# Revit family: Shower-Bath-American_Standard-SERIN-TU064500WDXH-02WDXH
name_source: partatom
category: Plumbing Fixtures
revit_build: Autodesk Revit 2014 (Build: 20130308_1515(x64)
units: mm (PartAtom-declared; Revit-internal decimal feet)

## types (2) — shared parameters
ADA Compliant = Yes
Assembly Code = D2020300
CW Connection = Yes
CWFU = 3
Cold Water Connection Diameter = 1/2"
Cold Water Connection Height = 44"
Cold Water Connection Radius = 1/4"
Default Elevation = 0"
Diverter_Shower Connection = 1/4"
Diverter_Shower Outlet Description = 1/2'' Global Outlet Connection
Finish = Metal-American Standard-002-Polished Chrome
HW Connection = Yes
HWFU = 3
Height = 78"
Hot Water Connection Diameter = 1/2"
Hot Water Connection Height = 44"
Hot Water Connection Radius = 1/4"
Installation Type = Wall Mounted
Length = 4 7/8"
Manufacturer = American Standard
Price = Prices may vary. Please consult Manufacturer Representative for most up-to-date price list.
Shower = Yes
Shower Connection Description = 1/2'' Global Inlet Connection
Shower Connection Size = 1/4"
Specification = Bath/shower fitting shall feature 3-function showerhead with Max. 2.5gpm/9.5L/min. flow rate. Shall feature double ceramic pressure balance cartridge which is capable of back-to-back installation. Cartridge shall feature integrated check valves to eliminate cross flow. Capable of meeting ASSE1016 @1.3gpm Cartridge shall also feature hot limit safety stop.
URL = http://www.americanstandard-us.com
Valve = Yes
Vent Connection = No
WFU = 4
Warranty Information = Limited Lifetime Function and Finish Warranty.
Waste Connection = No
Width = 7 1/4"

## per-type parameters (varying)
| type | Bath | Description | Diverter_Spout Connection | Diverter_Spout Outlet Description | Material | Spout Connection Description | Spout Connection Size |
| TU064502WDXH | Yes | TU064502WDXH Serin Bath/Shower Trim Kit with Pressure Balance Cartridge LESS Shwerhead. Lever handle. LESS valve body. | 1/4" | 1/2'' Global Outlet Connection | Brass-American Standard-002-Polished Chrome | 1/2'' Global Inlet Connection | 1/4" |
| TU064501WDXH | No | TU064501WDXH Serin Shower ONLY Trim Kit with Pressure Balance Cartridge LESS Shwerhead. Lever handle. LESS valve body. | 0" |  | Metal-American Standard-002-Polished Chrome |  | 0" |

note: column(s) folded — value = type name in every type: Model

## geometry (parser evidence)
native form markers: Sweep x3
no freeform markers — native parametric forms only
